# Revit family: Tambour Ellis 18  x 90
name_source: partatom
category: Generic Models
units: mm (PartAtom-declared; Revit-internal decimal feet)

## family parameters
Can host rebar = No
Cut with Voids When Loaded = No
Host = Face
Maintain Annotation Orientation = No
Part Type = Normal
Room Calculation Point = No
Round Connector Dimension = Use Diameter
Shared = No

## types (6) — shared parameters
Default Elevation = 4' - 0"

## per-type parameters (varying)
| type | Tambour Material |
| Tambour Ellis - 18 X 90 - OAK | Cambio Wood Veneer - Oak |
| Tambour Ellis - 18 X 90 - WALNUT | Cambio Wood Veneer - Walnut |
| Tambour Ellis - 18 X 90 - SW MATTE BLACK | Cambio Color Block - Tricorn Black |
| Tambour Ellis - 18 X 90 - SW MATTE WHITE | Cambio Color Block - White Flour |
| Tambour Ellis - 18 X 90 - SW MATTE GRAY | Cambio Color Block - Serious Gray |
| Tambour Ellis - 18 X 90 - SW MATTE LIGHT GRAY | Cambio Color Block - Morning Fog |

## geometry (parser evidence)
native form markers: Sweep x7
no freeform markers — native parametric forms only
